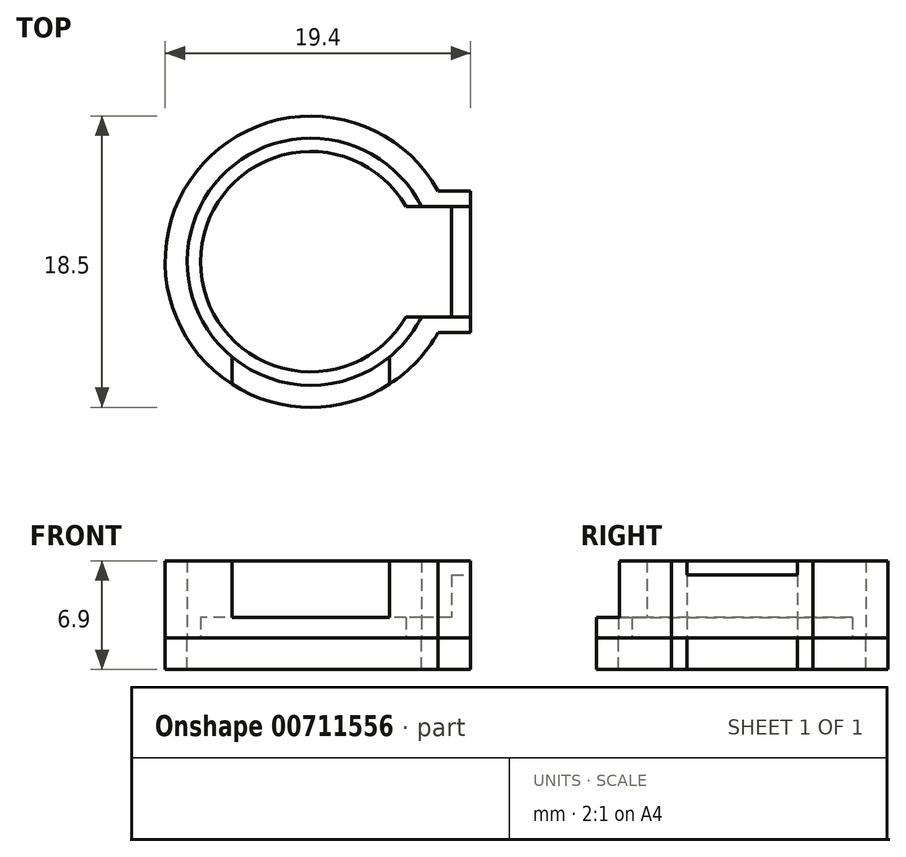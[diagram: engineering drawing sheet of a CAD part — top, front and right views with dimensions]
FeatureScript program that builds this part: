
annotation { "Feature Type Name" : "Feature", "Feature Type Description" : "" }
export const myFeature = defineFeature(function(context is Context, id is Id, definition is map)
    precondition{}
    {
        {
            var Q0;
            Q0=qCreatedBy(makeId("Top.planeOp"),FACE);
            var sketch = newSketch(context, id + "F0", { "sketchPlane" : qUnion([Q0])});
            skArc(sketch, "E0", {"start": v(7.03, 3.5) * mm, "mid": v(-7.85, 0) * mm, "end": v(7.03, -3.5) * mm});
            skLineSegment(sketch, "E1.bottom", {"start": v(8.95, 3.5) * mm, "end": v(6.75, 3.5) * mm});
            skLineSegment(sketch, "E1.top", {"start": v(8.95, -3.5) * mm, "end": v(6.75, -3.5) * mm});
            skLineSegment(sketch, "E1.left", {"start": v(8.95, 3.5) * mm, "end": v(8.95, -3.5) * mm});
            skPoint(sketch, "E1.middle", {"position": v(7.85, 0) * mm});
            skLineSegment(sketch, "E2", {"start": v(-7.85, 0) * mm, "end": v(-7.85, -7.8) * mm, "construction": true});
            skLineSegment(sketch, "E3", {"start": v(7.03, -3.5) * mm, "end": v(6.75, -3.5) * mm});
            skLineSegment(sketch, "E4", {"start": v(7.03, 3.5) * mm, "end": v(6.75, 3.5) * mm});
            skArc(sketch, "E5", {"start": v(8.08, 4.5) * mm, "mid": v(-9.25, 0) * mm, "end": v(8.08, -4.5) * mm});
            skLineSegment(sketch, "E6", {"start": v(8.08, 4.5) * mm, "end": v(10.15, 4.5) * mm});
            skLineSegment(sketch, "E7", {"start": v(10.15, 4.5) * mm, "end": v(10.15, -4.5) * mm});
            skLineSegment(sketch, "E8", {"start": v(10.15, -4.5) * mm, "end": v(8.08, -4.5) * mm});
            skLineSegment(sketch, "E9", {"start": v(-5, -6.05) * mm, "end": v(-5, -7.78) * mm});
            skLineSegment(sketch, "E10", {"start": v(5, -6.05) * mm, "end": v(5, -7.78) * mm});
            skLineSegment(sketch, "E11", {"start": v(8.95, 3.5) * mm, "end": v(10.15, 3.5) * mm});
            skLineSegment(sketch, "E12", {"start": v(8.95, -3.5) * mm, "end": v(10.15, -3.5) * mm});
            skCircle(sketch, "E13", {"center": v(0, 0) * mm, "radius": 7 * mm});
            skLineSegment(sketch, "E14", {"start": v(6.75, -3.5) * mm, "end": v(6.06, -3.5) * mm});
            skLineSegment(sketch, "E15", {"start": v(6.75, 3.5) * mm, "end": v(6.06, 3.5) * mm});
            skSolve(sketch);
        }
        {
            var Q0;
            Q0=qSketchRegion(id+"F0",true);
            var Q1;
            Q1=makeQuery(id+"F0.imprint","IMPRINT",FACE,{"disambiguationData":[TD([[makeQuery(id+"F0.imprint","IMPRINT",EDGE,{"derivedFrom":sQuery(id+"F0.wireOp",EDGE,"E1.bottom")}),1.0]])]});
            var Q2;
            {var subQ0=sQuery(id+"F0.wireOp",EDGE,"E13");var subQ1=makeQuery(id+"F0.imprint","INTERSECT",VERTEX,{"derivedFrom":[subQ0,sQuery(id+"F0.wireOp",EDGE,"E14")]});Q2=makeQuery(id+"F0.imprint","IMPRINT",FACE,{"disambiguationData":[TD([[makeQuery(id+"F0.imprint","IMPRINT",EDGE,{"disambiguationData":[TD([[subQ1,1.0]])],"derivedFrom":subQ0}),1.0]])]});}
            var Q3;
            {var subQ0=sQuery(id+"F0.wireOp",EDGE,"E3");Q3=makeQuery(id+"F0.imprint","IMPRINT",FACE,{"disambiguationData":[TD([[makeQuery(id+"F0.imprint","IMPRINT",EDGE,{"derivedFrom":subQ0}),1.0]])]});}
            extrude(context, id + "F1", {"entities" : qUnion([Q0, Q1, Q2, Q3]), "depth" : 1.3 * mm, "offsetDistance" : 25 * mm});
        }
        {
            var Q0;
            Q0=makeQuery(id+"F0.imprint","IMPRINT",FACE,{"disambiguationData":[TD([[makeQuery(id+"F0.imprint","IMPRINT",EDGE,{"derivedFrom":sQuery(id+"F0.wireOp",EDGE,"E1.bottom")}),-1.0]])]});
            var Q1;
            Q1=makeQuery(id+"F0.imprint","IMPRINT",FACE,{"disambiguationData":[TD([[makeQuery(id+"F0.imprint","IMPRINT",EDGE,{"derivedFrom":sQuery(id+"F0.wireOp",EDGE,"E1.top")}),1.0]])]});
            extrude(context, id + "F2", {"entities" : qUnion([Q0, Q1]), "operationType" : NewBodyOperationType.ADD, "depth" : 4.9 * mm, "offsetDistance" : 25 * mm});
        }
        {
            var Q0;
            Q0=makeQuery(id+"F0.imprint","IMPRINT",FACE,{"disambiguationData":[TD([[makeQuery(id+"F0.imprint","IMPRINT",EDGE,{"derivedFrom":sQuery(id+"F0.wireOp",EDGE,"E1.left")}),1.0]])]});
            extrude(context, id + "F3", {"entities" : qUnion([Q0]), "operationType" : NewBodyOperationType.ADD, "depth" : 4 * mm, "offsetDistance" : 25 * mm});
        }
        {
            var Q0;
            {var subQ3=sQuery(id+"F0.wireOp",EDGE,"E1.bottom");Q0=makeQuery(id+"F0.imprint","IMPRINT",FACE,{"disambiguationData":[TD([[makeQuery(id+"F0.imprint","IMPRINT",EDGE,{"derivedFrom":subQ3}),-1.0]])]});}
            var Q1;
            {var subQ0=sQuery(id+"F0.wireOp",EDGE,"E9");Q1=makeQuery(id+"F0.imprint","IMPRINT",FACE,{"disambiguationData":[TD([[makeQuery(id+"F0.imprint","IMPRINT",EDGE,{"derivedFrom":subQ0}),1.0]])]});}
            var Q2;
            {var subQ3=sQuery(id+"F0.wireOp",EDGE,"E1.top");Q2=makeQuery(id+"F0.imprint","IMPRINT",FACE,{"disambiguationData":[TD([[makeQuery(id+"F0.imprint","IMPRINT",EDGE,{"derivedFrom":subQ3}),1.0]])]});}
            var Q3;
            {var subQ0=sQuery(id+"F0.wireOp",EDGE,"E3");Q3=makeQuery(id+"F0.imprint","IMPRINT",FACE,{"disambiguationData":[TD([[makeQuery(id+"F0.imprint","IMPRINT",EDGE,{"derivedFrom":subQ0}),1.0]])]});}
            extrude(context, id + "F4", {"entities" : qUnion([Q0, Q1, Q2, Q3]), "oppositeDirection" : true, "depth" : 2 * mm, "offsetDistance" : 25 * mm});
        }
    });
